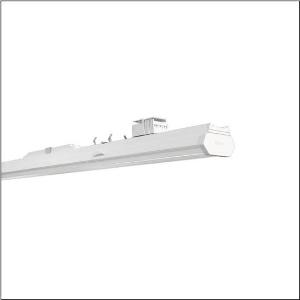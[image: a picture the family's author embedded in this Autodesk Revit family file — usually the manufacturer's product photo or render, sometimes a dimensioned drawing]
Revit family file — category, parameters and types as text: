
# Revit family: licross_11_protected_mo_51td1b7n48xg
name_source: partatom
category: Lighting Fixtures
units: mm (PartAtom-declared; Revit-internal decimal feet)

## family parameters
Cut with Voids When Loaded = No
Host = Face
Light Source = No
Part Type = Normal
Room Calculation Point = No
Round Connector Dimension = Use Diameter
Shared = No

## types (1)
- Licross 11 Protected MO (1 x LED, 8190 lm, 48.6 W, 4000K)
    Apparent Load = 49 VA
    CIE Flux Codes = 54 82 95 97 100
    Color Rendering = 80
    Color Temperature = 4000K
    Default Elevation = 1800 mm
    Description = Licross 11 Protected MO, luminaire insert, of sheet steel, galvanised, coil coated, white, length: 1.500mm, width: 90mm, height: 101mm, LED rated luminous flux: 8.190lm, light colour: 840, SDCM (Standard Deviation of Colour Matching)MacAdam ≤ 2 SDCM (initial), control gear: ON/OFF, with plug, 3-pole, with phase selection, mains connection: 220..240V, AC, 50/60Hz, rated input power: 49W, internal wiring halogen-free, primary optical cover: cover, of PMMA, light emission: direct distribution, primary light characteristic: symmetric, protection rating (complete): IP54, insulation class (complete): insulation class I (protective earthing), certification: CE, ENEC, VDE, UKCA, protection symbol: D if used in an environment with non-conductive dust loads with corresponding accessories, impact resistance: IK06, permissible ambient temperature for indoor applications: -25..+35°C, corresponds to IFS (International Featured Standards) requirements for safety and quality in the food industry, reducing of maximum allowable ambient temperature of 5°C with ceiling mounting, LABS conformity tested according to VDMA 24364:2018-05, The light source and the operating device comply with the requirements of the Ecodesign Regulation (EU) 2019/2020 and are replaceable in accordance with this regulation, packaging unit: 1 piece
    Height = 92 mm
    Lamp = 1 x LED
    Lamp Light Flux = 8190 lm
    Lamp Power = 48.6 W
    Lamp count = 1
    Length = 1500 mm
    Luminous efficacy = 169 lm/W
    Manufacturer = Siteco
    ModVariant = No
    Model = 51TD1B7N48XG
    Mounting Place = Ceiling
    Mounting Type = Pendant
    Number of Poles = 1
    OnlyDefault = Yes
    Power Factor = 1
    Product Name = Licross 11 Protected MO
    Product group = luminaire insert | ceiling pendant
    ProductGroupID = 901
    Protection Class = Protection class I
    Protection Degree = IP 54
    RLX_Detail_Level = 1
    RLX_Emergency_Light_Flux = 0 lm
    RLX_Emergency_Type = 0
    RLX_Emergency_Type_DB = No
    RlxData = <blob elided: 20897 chars, md5=cbc1933b>
    Socket = socket
    Standby Power = 0 W
    System Light Flux = 8190 lm
    System Power = 49 W
    Type Comments = Product without accessories
    Type Image = l_1256145.jpg
    URL = http://relux.com
    VarID = ---
    Voltage = 0 V
    Weight = 0.00 kg
    Width = 88 mm

## geometry (parser evidence)
native form markers: Blend x4, Sweep x12
no freeform markers — native parametric forms only
